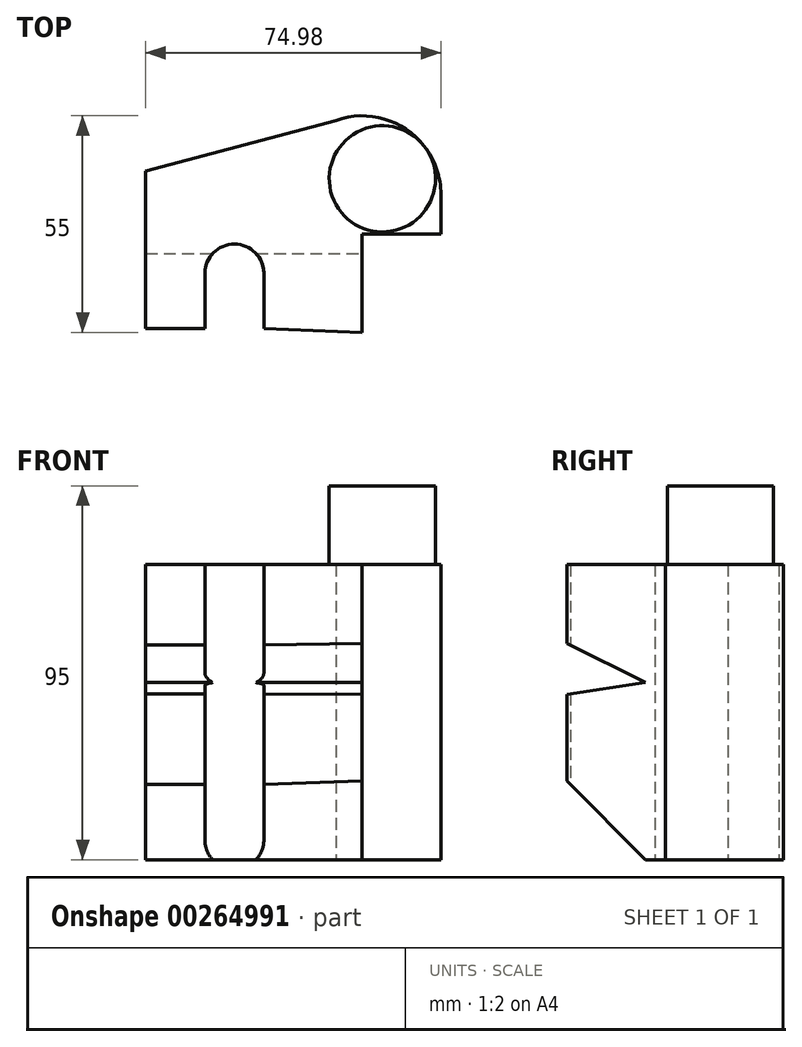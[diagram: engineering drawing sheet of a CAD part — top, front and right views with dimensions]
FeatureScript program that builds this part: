
annotation { "Feature Type Name" : "Feature", "Feature Type Description" : "" }
export const myFeature = defineFeature(function(context is Context, id is Id, definition is map)
    precondition{}
    {
        {
            var Q0;
            Q0=qCreatedBy(makeId("Top.planeOp"),FACE);
            var sketch = newSketch(context, id + "F0", { "sketchPlane" : qUnion([Q0])});
            skPoint(sketch, "E0.middle", {"position": v(0, 0) * mm});
            skLineSegment(sketch, "E1", {"start": v(-37.5, -19.1) * mm, "end": v(-22.5, -19.1) * mm});
            skLineSegment(sketch, "E2", {"start": v(-22.5, -19.1) * mm, "end": v(-22.5, -5.1) * mm});
            skLineSegment(sketch, "E3", {"start": v(-7.5, -5.1) * mm, "end": v(-7.5, -19.1) * mm});
            skLineSegment(sketch, "E4", {"start": v(-7.5, -19.1) * mm, "end": v(17.48, -20) * mm});
            skLineSegment(sketch, "E5", {"start": v(17.48, -20) * mm, "end": v(17.48, 5) * mm});
            skLineSegment(sketch, "E6", {"start": v(-37.5, -19.1) * mm, "end": v(-37.5, 20.9) * mm});
            skArc(sketch, "E7", {"start": v(-7.5, -5.1) * mm, "mid": v(-15, 2.4) * mm, "end": v(-22.5, -5.1) * mm});
            skLineSegment(sketch, "E8", {"start": v(17.48, 5) * mm, "end": v(37.48, 5) * mm});
            skLineSegment(sketch, "E9", {"start": v(37.48, 5) * mm, "end": v(37.48, 15) * mm});
            skArc(sketch, "E10", {"start": v(37.48, 15) * mm, "mid": v(29.02, 31.34) * mm, "end": v(10.8, 33.85) * mm});
            skLineSegment(sketch, "E11", {"start": v(10.8, 33.85) * mm, "end": v(-37.5, 20.9) * mm});
            skSolve(sketch);
        }
        {
            var Q0;
            Q0 = qSketchRegion(id + "F0", true);
            extrude(context, id + "F1", {"entities" : qUnion([Q0]), "depth" : 75 * mm});
        }
        {
            var Q0;
            Q0=makeQuery(id+"F1.opExtrude","SWEPT_FACE",FACE,{"disambiguationData":[OSD([sQuery(id+"F0.wireOp",EDGE,"E5")])]});
            var sketch = newSketch(context, id + "F2", { "sketchPlane" : qUnion([Q0])});
            skLineSegment(sketch, "E12", {"start": v(0, 45) * mm, "end": v(-20, 55) * mm});
            skLineSegment(sketch, "E13", {"start": v(-20, 55) * mm, "end": v(-20, 42.03) * mm});
            skLineSegment(sketch, "E14", {"start": v(0, 45) * mm, "end": v(-20, 42.03) * mm});
            skSolve(sketch);
        }
        {
            var Q0;
            Q0=makeQuery(id+"F2.imprint","IMPRINT",FACE,{"disambiguationData":[TD([[makeQuery(id+"F2.imprint","IMPRINT",EDGE,{"derivedFrom":sQuery(id+"F2.wireOp",EDGE,"E12")}),1.0]])]});
            extrude(context, id + "F3", {"entities" : qUnion([Q0]), "operationType" : NewBodyOperationType.REMOVE, "oppositeDirection" : true, "depth" : 75 * mm});
        }
        {
            var Q0;
            Q0=makeQuery(id+"F1.opExtrude","SWEPT_FACE",FACE,{"disambiguationData":[OSD([sQuery(id+"F0.wireOp",EDGE,"E5")])]});
            var sketch = newSketch(context, id + "F4", { "sketchPlane" : qUnion([Q0])});
            skLineSegment(sketch, "E15", {"start": v(-20, 0) * mm, "end": v(0, 0) * mm});
            skLineSegment(sketch, "E16", {"start": v(-20, 0) * mm, "end": v(-20, 20) * mm});
            skLineSegment(sketch, "E17", {"start": v(-20, 20) * mm, "end": v(0, 0) * mm});
            skSolve(sketch);
        }
        {
            var Q0;
            Q0=makeQuery(id+"F4.imprint","IMPRINT",FACE,{"disambiguationData":[TD([[makeQuery(id+"F4.imprint","IMPRINT",EDGE,{"derivedFrom":sQuery(id+"F4.wireOp",EDGE,"E15")}),1.0]])]});
            extrude(context, id + "F5", {"entities" : qUnion([Q0]), "operationType" : NewBodyOperationType.REMOVE, "oppositeDirection" : true, "depth" : 75 * mm});
        }
        {
            var Q0;
            Q0=makeQuery(id+"F1.opExtrude","CAP_FACE",FACE,{"disambiguationData":[OSD([sQuery(id+"F0.wireOp",EDGE,"E1"),sQuery(id+"F0.wireOp",EDGE,"E2"),sQuery(id+"F0.wireOp",EDGE,"E3"),sQuery(id+"F0.wireOp",EDGE,"E4"),sQuery(id+"F0.wireOp",EDGE,"E5"),sQuery(id+"F0.wireOp",EDGE,"E6"),sQuery(id+"F0.wireOp",EDGE,"E7"),sQuery(id+"F0.wireOp",EDGE,"E8"),sQuery(id+"F0.wireOp",EDGE,"E9"),sQuery(id+"F0.wireOp",EDGE,"E10"),sQuery(id+"F0.wireOp",EDGE,"E11")])],"isStart":false});
            var sketch = newSketch(context, id + "F6", { "sketchPlane" : qUnion([Q0])});
            skCircle(sketch, "E18", {"center": v(22.6, 19) * mm, "radius": 13.5 * mm});
            skSolve(sketch);
        }
        {
            var Q0;
            Q0=makeQuery(id+"F6.imprint","IMPRINT",FACE,{"disambiguationData":[TD([[makeQuery(id+"F6.imprint","IMPRINT",EDGE,{"derivedFrom":sQuery(id+"F6.wireOp",EDGE,"E18")}),1.0]])]});
            extrude(context, id + "F7", {"entities" : qUnion([Q0]), "operationType" : NewBodyOperationType.ADD, "depth" : 20 * mm});
        }
    });
